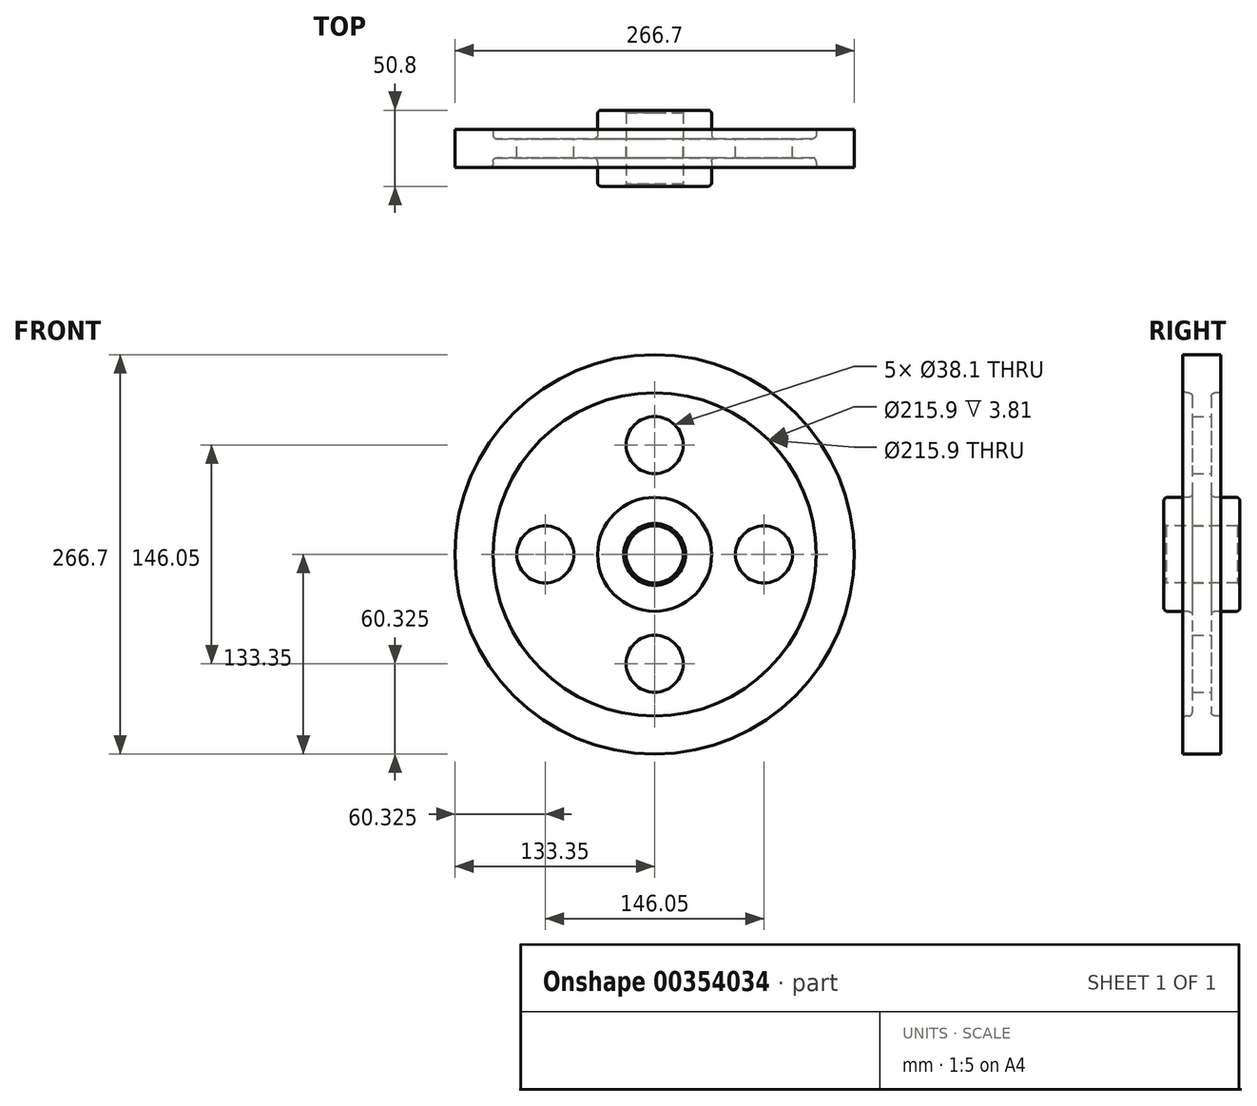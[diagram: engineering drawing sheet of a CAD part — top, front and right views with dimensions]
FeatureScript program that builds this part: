
annotation { "Feature Type Name" : "Feature", "Feature Type Description" : "" }
export const myFeature = defineFeature(function(context is Context, id is Id, definition is map)
    precondition{}
    {
        {
            var Q0;
            Q0=qCreatedBy(makeId("Right.planeOp"),FACE);
            var sketch = newSketch(context, id + "F0", { "sketchPlane" : qUnion([Q0])});
            skLineSegment(sketch, "E0", {"start": v(0, 0) * mm, "end": v(76.5, 0) * mm, "construction": true});
            skLineSegment(sketch, "E1.0", {"start": v(6.35, 38.1) * mm, "end": v(25.4, 38.1) * mm});
            skLineSegment(sketch, "E2.0", {"start": v(0, 19.05) * mm, "end": v(25.4, 19.05) * mm});
            skLineSegment(sketch, "E3.0", {"start": v(6.35, 107.95) * mm, "end": v(12.7, 107.95) * mm});
            skLineSegment(sketch, "E4.0", {"start": v(0, 133.35) * mm, "end": v(12.7, 133.35) * mm});
            skLineSegment(sketch, "E5", {"start": v(0, 133.35) * mm, "end": v(0, 0) * mm, "construction": true});
            skLineSegment(sketch, "E6.0", {"start": v(25.4, 38.1) * mm, "end": v(25.4, 19.05) * mm});
            skLineSegment(sketch, "E7.0", {"start": v(6.35, 107.95) * mm, "end": v(6.35, 38.1) * mm});
            skLineSegment(sketch, "E8.0", {"start": v(12.7, 133.35) * mm, "end": v(12.7, 107.95) * mm});
            skLineSegment(sketch, "E9.MirrorCS", {"start": v(-6.35, 133.35) * mm, "end": v(-6.35, 19.05) * mm});
            skLineSegment(sketch, "E10.MirrorCS", {"start": v(-12.7, 133.35) * mm, "end": v(-12.7, 107.95) * mm});
            skLineSegment(sketch, "E11.MirrorCS", {"start": v(0, 107.95) * mm, "end": v(-12.7, 107.95) * mm});
            skLineSegment(sketch, "E12.MirrorCS", {"start": v(0, 38.1) * mm, "end": v(-25.4, 38.1) * mm});
            skLineSegment(sketch, "E13.MirrorCS", {"start": v(-25.4, 38.1) * mm, "end": v(-25.4, 19.05) * mm});
            skPoint(sketch, "E14.orphan", {"position": v(25.4, 0) * mm});
            skPoint(sketch, "E15.orphan", {"position": v(6.35, 0) * mm});
            skPoint(sketch, "E16.orphan", {"position": v(0, 38.1) * mm});
            skPoint(sketch, "E17.orphan", {"position": v(0, 107.95) * mm});
            skPoint(sketch, "E18.orphan", {"position": v(6.35, 133.35) * mm});
            skLineSegment(sketch, "E19.MirrorCS", {"start": v(0, 133.35) * mm, "end": v(-12.7, 133.35) * mm});
            skLineSegment(sketch, "E20.MirrorCS", {"start": v(0, 19.05) * mm, "end": v(-25.4, 19.05) * mm});
            skPoint(sketch, "E21.orphan", {"position": v(-25.4, 0) * mm});
            skPoint(sketch, "E22.orphan", {"position": v(-6.35, 0) * mm});
            skSolve(sketch);
        }
        {
            var Q0;
            {var subQ5=sQuery(id+"F0.wireOp",EDGE,"E13.MirrorCS");Q0=makeQuery(id+"F0.imprint","IMPRINT",FACE,{"disambiguationData":[TD([[makeQuery(id+"F0.imprint","IMPRINT",EDGE,{"derivedFrom":subQ5}),1.0]])]});}
            var Q1;
            Q1=makeQuery(id+"F0.imprint","IMPRINT",FACE,{"disambiguationData":[TD([[makeQuery(id+"F0.imprint","IMPRINT",EDGE,{"derivedFrom":sQuery(id+"F0.wireOp",EDGE,"E1.0")}),-1.0]])]});
            var Q2;
            {var subQ5=sQuery(id+"F0.wireOp",EDGE,"E10.MirrorCS");Q2=makeQuery(id+"F0.imprint","IMPRINT",FACE,{"disambiguationData":[TD([[makeQuery(id+"F0.imprint","IMPRINT",EDGE,{"derivedFrom":subQ5}),1.0]])]});}
            var Q3;
            Q3=sQuery(id+"F0.wireOp",EDGE,"E0");
            revolve(context, id + "F1", {"entities" : qUnion([Q0, Q1, Q2]), "axis" : qUnion([Q3]), "revolveType" : RevolveType.FULL});
        }
        {
            var Q0;
            Q0=makeQuery(id+"F1.opRevolve","SWEPT_FACE",FACE,{"disambiguationData":[OSD([sQuery(id+"F0.wireOp",EDGE,"E7.0")])]});
            var sketch = newSketch(context, id + "F2", { "sketchPlane" : qUnion([Q0])});
            skLineSegment(sketch, "E23", {"start": v(0, 0) * mm, "end": v(0, 73.03) * mm});
            skCircle(sketch, "E24", {"center": v(0, 73.03) * mm, "radius": 19.05 * mm});
            skLineSegment(sketch, "E25.direction1", {"start": v(0, 73.03) * mm, "end": v(25.4, 73.03) * mm, "construction": true});
            skCircle(sketch, "E26.1.0", {"center": v(-73.03, 0) * mm, "radius": 19.05 * mm});
            skCircle(sketch, "E26.2.0", {"center": v(0, -73.03) * mm, "radius": 19.05 * mm});
            skCircle(sketch, "E26.3.0", {"center": v(73.03, 0) * mm, "radius": 19.05 * mm});
            skPoint(sketch, "E26.center", {"position": v(0, 0) * mm});
            skSolve(sketch);
        }
        {
            var Q0;
            Q0=makeQuery(id+"F2.imprint","IMPRINT",FACE,{"disambiguationData":[TD([[makeQuery(id+"F2.imprint","IMPRINT",EDGE,{"derivedFrom":sQuery(id+"F2.wireOp",EDGE,"E24")}),1.0]])]});
            var Q1;
            Q1=makeQuery(id+"F2.imprint","IMPRINT",FACE,{"disambiguationData":[TD([[makeQuery(id+"F2.imprint","IMPRINT",EDGE,{"derivedFrom":sQuery(id+"F2.wireOp",EDGE,"E26.1.0")}),1.0]])]});
            var Q2;
            Q2=makeQuery(id+"F2.imprint","IMPRINT",FACE,{"disambiguationData":[TD([[makeQuery(id+"F2.imprint","IMPRINT",EDGE,{"derivedFrom":sQuery(id+"F2.wireOp",EDGE,"E26.2.0")}),1.0]])]});
            extrude(context, id + "F3", {"entities" : qUnion([Q0, Q1, Q2]), "operationType" : NewBodyOperationType.REMOVE, "oppositeDirection" : true, "depth" : 25.4 * mm});
        }
        {
            var Q0;
            Q0=makeQuery(id+"F2.imprint","IMPRINT",FACE,{"disambiguationData":[TD([[makeQuery(id+"F2.imprint","IMPRINT",EDGE,{"derivedFrom":sQuery(id+"F2.wireOp",EDGE,"E26.3.0")}),1.0]])]});
            extrude(context, id + "F4", {"entities" : qUnion([Q0]), "operationType" : NewBodyOperationType.REMOVE, "oppositeDirection" : true, "depth" : 25.4 * mm});
        }
        {
            var Q0;
            Q0=makeQuery(id+"F1.opRevolve","SWEPT_EDGE",EDGE,{"disambiguationData":[OSD([sQuery(id+"F0.wireOp",EDGE,"E9.MirrorCS"),sQuery(id+"F0.wireOp",EDGE,"E12.MirrorCS")])]});
            var Q1;
            Q1=makeQuery(id+"F1.opRevolve","SWEPT_EDGE",EDGE,{"disambiguationData":[OSD([sQuery(id+"F0.wireOp",EDGE,"E12.MirrorCS"),sQuery(id+"F0.wireOp",EDGE,"E13.MirrorCS")])]});
            var Q2;
            Q2=makeQuery(id+"F1.opRevolve","SWEPT_EDGE",EDGE,{"disambiguationData":[OSD([sQuery(id+"F0.wireOp",EDGE,"E9.MirrorCS"),sQuery(id+"F0.wireOp",EDGE,"E11.MirrorCS")])]});
            var Q3;
            Q3=makeQuery(id+"F1.opRevolve","SWEPT_EDGE",EDGE,{"disambiguationData":[OSD([sQuery(id+"F0.wireOp",EDGE,"E10.MirrorCS"),sQuery(id+"F0.wireOp",EDGE,"E11.MirrorCS")])]});
            var Q4;
            Q4=makeQuery(id+"F1.opRevolve","SWEPT_EDGE",EDGE,{"disambiguationData":[OSD([sQuery(id+"F0.wireOp",EDGE,"E1.0"),sQuery(id+"F0.wireOp",EDGE,"E7.0")])]});
            var Q5;
            Q5=makeQuery(id+"F1.opRevolve","SWEPT_EDGE",EDGE,{"disambiguationData":[OSD([sQuery(id+"F0.wireOp",EDGE,"E1.0"),sQuery(id+"F0.wireOp",EDGE,"E6.0")])]});
            var Q6;
            Q6=makeQuery(id+"F1.opRevolve","SWEPT_EDGE",EDGE,{"disambiguationData":[OSD([sQuery(id+"F0.wireOp",EDGE,"E3.0"),sQuery(id+"F0.wireOp",EDGE,"E7.0")])]});
            fillet(context, id + "F5", {"entities" : qUnion([Q0, Q1, Q2, Q3, Q4, Q5, Q6]), "radius" : 2.54 * mm, "tangentPropagation" : true, "allowEdgeOverflow" : false});
        }
        {
            var Q0;
            Q0=makeQuery(id+"F1.opRevolve","SWEPT_EDGE",EDGE,{"disambiguationData":[OSD([sQuery(id+"F0.wireOp",EDGE,"E13.MirrorCS"),sQuery(id+"F0.wireOp",EDGE,"E20.MirrorCS")])]});
            var Q1;
            Q1=makeQuery(id+"F1.opRevolve","SWEPT_EDGE",EDGE,{"disambiguationData":[OSD([sQuery(id+"F0.wireOp",EDGE,"E2.0"),sQuery(id+"F0.wireOp",EDGE,"E6.0")])]});
            chamfer(context, id + "F6", {"entities" : qUnion([Q0, Q1]), "width" : 1.59 * mm, "tangentPropagation" : true});
        }
    });
